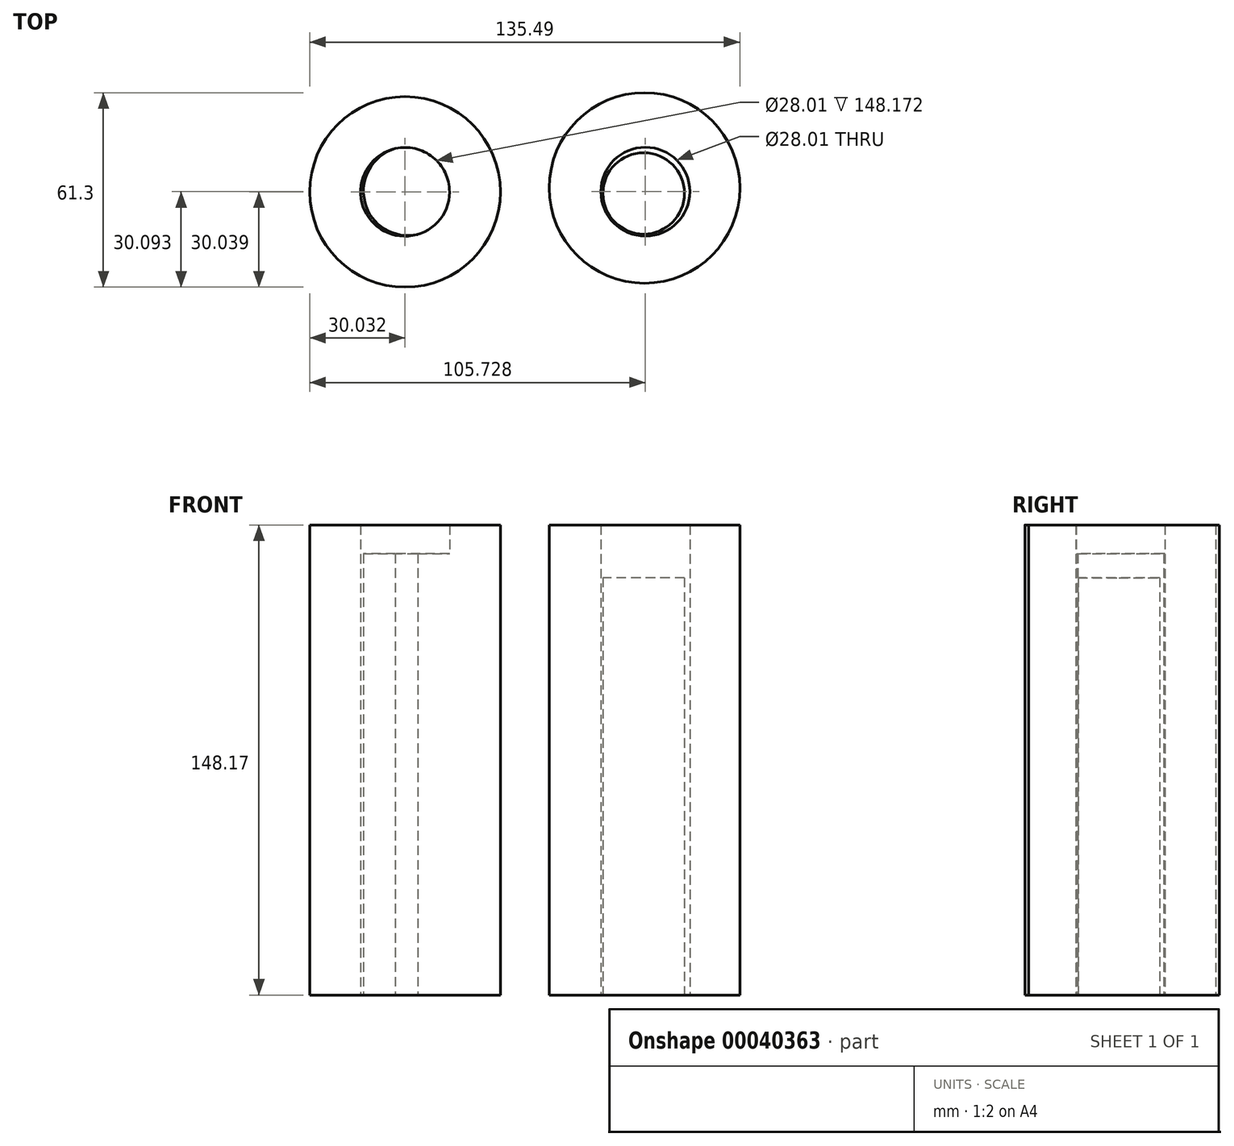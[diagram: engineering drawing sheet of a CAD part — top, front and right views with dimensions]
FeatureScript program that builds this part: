
annotation { "Feature Type Name" : "Feature", "Feature Type Description" : "" }
export const myFeature = defineFeature(function(context is Context, id is Id, definition is map)
    precondition{}
    {
        {
            var Q0;
            Q0=qCreatedBy(makeId("Top.planeOp"),FACE);
            var sketch = newSketch(context, id + "F0", { "sketchPlane" : qUnion([Q0])});
            skCircle(sketch, "E0", {"center": v(-35.88, 29.9) * mm, "radius": 30.04 * mm});
            skPoint(sketch, "E0.first.point", {"position": v(-6.46, 23.86) * mm});
            skPoint(sketch, "E0.second.point", {"position": v(-65.65, 33.9) * mm});
            skPoint(sketch, "E0.third.point", {"position": v(-38.74, 0) * mm});
            skCircle(sketch, "E1", {"center": v(39.54, 31.12) * mm, "radius": 30.04 * mm});
            skPoint(sketch, "E1.first.point", {"position": v(68.97, 25.08) * mm});
            skPoint(sketch, "E1.second.point", {"position": v(9.78, 35.12) * mm});
            skPoint(sketch, "E1.third.point", {"position": v(36.68, 1.22) * mm});
            skCircle(sketch, "E2", {"center": v(-35.88, 29.9) * mm, "radius": 14 * mm});
            skCircle(sketch, "E3", {"center": v(39.82, 29.95) * mm, "radius": 14 * mm});
            skSolve(sketch);
        }
        {
            var Q0;
            Q0 = qSketchRegion(id + "F0", true);
            extrude(context, id + "F1", {"entities" : qUnion([Q0]), "depth" : 148.17 * mm});
        }
        {
            var Q0;
            Q0=qCreatedBy(makeId("Top.planeOp"),FACE);
            var sketch = newSketch(context, id + "F2", { "sketchPlane" : qUnion([Q0])});
            skCircle(sketch, "E4", {"center": v(39.28, 29.42) * mm, "radius": 12.83 * mm});
            skCircle(sketch, "E5", {"center": v(-34.98, 30.13) * mm, "radius": 14 * mm});
            skSolve(sketch);
        }
        {
            var Q0;
            Q0=makeQuery(id+"F2.imprint","IMPRINT",FACE,{"disambiguationData":[TD([[makeQuery(id+"F2.imprint","IMPRINT",EDGE,{"derivedFrom":sQuery(id+"F2.wireOp",EDGE,"E4")}),1.0]])]});
            extrude(context, id + "F3", {"entities" : qUnion([Q0]), "depth" : 131.58 * mm});
        }
        {
            var Q0;
            Q0=makeQuery(id+"F2.imprint","IMPRINT",FACE,{"disambiguationData":[TD([[makeQuery(id+"F2.imprint","IMPRINT",EDGE,{"derivedFrom":sQuery(id+"F2.wireOp",EDGE,"E5")}),1.0]])]});
            extrude(context, id + "F4", {"entities" : qUnion([Q0]), "operationType" : NewBodyOperationType.ADD, "depth" : 139.11 * mm});
        }
    });
